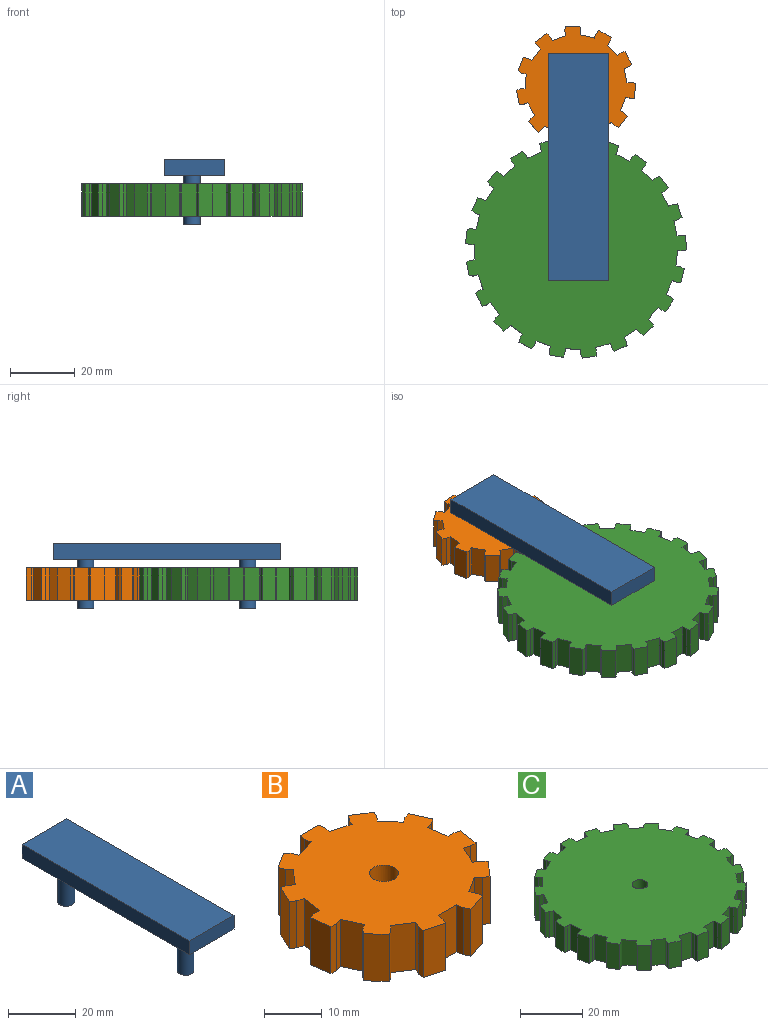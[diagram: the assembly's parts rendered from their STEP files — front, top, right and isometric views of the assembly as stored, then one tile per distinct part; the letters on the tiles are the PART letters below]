
ASSEMBLY  parts=3 mates=2
PART A: 10 faces, bbox 18.7x70.1x20 mm
  f0: plane 18.73x5mm, normal (0,1,0), area 93.7mm2, adj f1,f3,f4,f5
  f1: plane 70.05x5mm, normal (-1,0,0), area 350.3mm2, adj f0,f2,f4,f5
  f2: plane 18.73x5mm, normal (0,-1,0), area 93.7mm2, adj f1,f3,f4,f5
  f3: plane 70.05x5mm, normal (1,0,0), area 350.3mm2, adj f0,f2,f4,f5
  f4: plane 70.05x18.73mm, normal (0,0,1), area 1312.1mm2, adj f0,f1,f2,f3
  f5: plane 70.05x18.73mm, normal (0,0,-1), area 1272.8mm2, adj f0,f1,f2,f3,f6,f8
  f6: cylinder r=2.5mm len=15mm, axis (0,0,1), area 235.6mm2, adj f5,f7
  f7: plane 5x5mm, normal (0,0,-1), area 19.6mm2, adj f6
  f8: cylinder r=2.5mm len=15mm, axis (0,0,1), area 235.6mm2, adj f5,f9
  f9: plane 5x5mm, normal (0,0,-1), area 19.6mm2, adj f8
PART B: 69 faces, bbox 36.9x36.5x10 mm
  f0: plane 10x1.43mm, normal (-0.99,-0.14,0), area 14.5mm2, adj f1,f6,f7,f14
  f1: plane 10x1.18mm, normal (-0.9,-0.43,0), area 13mm2, adj f0,f2,f6,f7
  f2: plane 10x4.31mm, normal (0.28,-0.96,0), area 44.9mm2, adj f1,f3,f6,f7
  f3: plane 10x1.29mm, normal (0.99,0.13,0), area 13mm2, adj f2,f4,f6,f7
  f4: plane 10x1.32mm, normal (0.91,0.42,0), area 14.5mm2, adj f3,f5,f6,f7
  f5: plane 10x3.77mm, normal (0.54,-0.84,0), area 44.8mm2, adj f4,f6,f7,f8
  f6: plane 36.87x36.49mm, normal (0,0,1), area 888.5mm2, adj f0,f1,f2,f3,f4,f5,f8,f9
  f7: plane 36.87x36.49mm, normal (0,0,-1), area 888.5mm2, adj f0,f1,f2,f3,f4,f5,f8,f9
  f8: plane 10x1.09mm, normal (-0.76,-0.65,0), area 14.5mm2, adj f5,f6,f7,f63
  f9: plane 10x1.32mm, normal (-0.91,0.42,0), area 14.5mm2, adj f6,f7,f10,f20
  f10: plane 10x1.29mm, normal (-0.99,0.13,0), area 13mm2, adj f6,f7,f9,f11
  f11: plane 10x4.31mm, normal (-0.28,-0.96,0), area 44.9mm2, adj f6,f7,f10,f12
  f12: plane 10x1.18mm, normal (0.9,-0.43,0), area 13mm2, adj f6,f7,f11,f13
  f13: plane 10x1.43mm, normal (0.99,-0.14,0), area 14.5mm2, adj f6,f7,f12,f14
  f14: plane 10x4.48mm, normal (0,-1,0), area 44.8mm2, adj f0,f6,f7,f13
  f15: plane 10x1.22mm, normal (-0.54,0.84,0), area 14.5mm2, adj f6,f7,f16,f26
  f16: plane 10x0.99mm, normal (-0.76,0.65,0), area 13mm2, adj f6,f7,f15,f17
  f17: plane 10x3.4mm, normal (-0.76,-0.65,0), area 44.9mm2, adj f6,f7,f16,f18
  f18: plane 10x1.1mm, normal (0.53,-0.85,0), area 13mm2, adj f6,f7,f17,f19
  f19: plane 10x1.09mm, normal (0.76,-0.65,0), area 14.5mm2, adj f6,f7,f18,f20
  f20: plane 10x3.77mm, normal (-0.54,-0.84,0), area 44.8mm2, adj f6,f7,f9,f19
  f21: plane 10x1.45mm, normal (0,1,0), area 14.5mm2, adj f6,f7,f22,f32
  f22: plane 10x1.25mm, normal (-0.29,0.96,0), area 13mm2, adj f6,f7,f21,f23
  f23: plane 10x4.45mm, normal (-0.99,-0.14,0), area 44.9mm2, adj f6,f7,f22,f24
  f24: plane 10x1.3mm, normal (-0.01,-1,0), area 13mm2, adj f6,f7,f23,f25
  f25: plane 10x1.39mm, normal (0.28,-0.96,0), area 14.5mm2, adj f6,f7,f24,f26
  f26: plane 10x4.08mm, normal (-0.91,-0.42,0), area 44.8mm2, adj f6,f7,f15,f25
  f27: plane 10x1.22mm, normal (0.54,0.84,0), area 14.5mm2, adj f6,f7,f28,f38
  f28: plane 10x1.25mm, normal (0.27,0.96,0), area 13mm2, adj f6,f7,f27,f29
  f29: plane 10x4.09mm, normal (-0.91,0.42,0), area 44.9mm2, adj f6,f7,f28,f30
  f30: plane 10x1.09mm, normal (-0.55,-0.84,0), area 13mm2, adj f6,f7,f29,f31
  f31: plane 10x1.39mm, normal (-0.28,-0.96,0), area 14.5mm2, adj f6,f7,f30,f32
  f32: plane 10x4.44mm, normal (-0.99,0.14,0), area 44.8mm2, adj f6,f7,f21,f31
  f33: plane 10x1.32mm, normal (0.91,0.42,0), area 14.5mm2, adj f6,f7,f34,f44
  f34: plane 10x0.98mm, normal (0.75,0.66,0), area 13mm2, adj f6,f7,f33,f35
  f35: plane 10x3.78mm, normal (-0.54,0.84,0), area 44.9mm2, adj f6,f7,f34,f36
  f36: plane 10x1.19mm, normal (-0.91,-0.41,0), area 13mm2, adj f6,f7,f35,f37
  f37: plane 10x1.09mm, normal (-0.76,-0.65,0), area 14.5mm2, adj f6,f7,f36,f38
  f38: plane 10x3.39mm, normal (-0.76,0.65,0), area 44.8mm2, adj f6,f7,f27,f37
  f39: plane 10x1.43mm, normal (0.99,-0.14,0), area 14.5mm2, adj f6,f7,f40,f50
  f40: plane 10x1.29mm, normal (0.99,0.15,0), area 13mm2, adj f6,f7,f39,f41
  f41: plane 10x4.49mm, normal (0,1,0), area 44.9mm2, adj f6,f7,f40,f42
  f42: plane 10x1.29mm, normal (-0.99,0.15,0), area 13mm2, adj f6,f7,f41,f43
  f43: plane 10x1.43mm, normal (-0.99,-0.14,0), area 14.5mm2, adj f6,f7,f42,f44
  f44: plane 10x4.3mm, normal (-0.28,0.96,0), area 44.8mm2, adj f6,f7,f33,f43
  f45: plane 10x1.09mm, normal (0.76,-0.65,0), area 14.5mm2, adj f6,f7,f46,f56
  f46: plane 10x1.19mm, normal (0.91,-0.41,0), area 13mm2, adj f6,f7,f45,f47
  f47: plane 10x3.78mm, normal (0.54,0.84,0), area 44.9mm2, adj f6,f7,f46,f48
  f48: plane 10x0.98mm, normal (-0.75,0.66,0), area 13mm2, adj f6,f7,f47,f49
  f49: plane 10x1.32mm, normal (-0.91,0.42,0), area 14.5mm2, adj f6,f7,f48,f50
  f50: plane 10x4.3mm, normal (0.28,0.96,0), area 44.8mm2, adj f6,f7,f39,f49
  f51: plane 10x1.39mm, normal (0.28,-0.96,0), area 14.5mm2, adj f6,f7,f52,f62
  f52: plane 10x1.09mm, normal (0.55,-0.84,0), area 13mm2, adj f6,f7,f51,f53
  f53: plane 10x4.09mm, normal (0.91,0.42,0), area 44.9mm2, adj f6,f7,f52,f54
  f54: plane 10x1.25mm, normal (-0.27,0.96,0), area 13mm2, adj f6,f7,f53,f55
  f55: plane 10x1.22mm, normal (-0.54,0.84,0), area 14.5mm2, adj f6,f7,f54,f56
  f56: plane 10x3.39mm, normal (0.76,0.65,0), area 44.8mm2, adj f6,f7,f45,f55
  f57: plane 10x1.39mm, normal (-0.28,-0.96,0), area 14.5mm2, adj f6,f7,f58,f67
  f58: plane 10x1.3mm, normal (0.01,-1,0), area 13mm2, adj f6,f7,f57,f59
  f59: plane 10x4.45mm, normal (0.99,-0.14,0), area 44.9mm2, adj f6,f7,f58,f60
  f60: plane 10x1.25mm, normal (0.29,0.96,0), area 13mm2, adj f6,f7,f59,f61
  f61: plane 10x1.45mm, normal (0,1,0), area 14.5mm2, adj f6,f7,f60,f62
  f62: plane 10x4.44mm, normal (0.99,0.14,0), area 44.8mm2, adj f6,f7,f51,f61
  f63: plane 10x1.1mm, normal (-0.53,-0.85,0), area 13mm2, adj f6,f7,f8,f64
  f64: plane 10x3.4mm, normal (0.76,-0.65,0), area 44.9mm2, adj f6,f7,f63,f65
  f65: plane 10x0.99mm, normal (0.76,0.65,0), area 13mm2, adj f6,f7,f64,f66
  f66: plane 10x1.22mm, normal (0.54,0.84,0), area 14.5mm2, adj f6,f7,f65,f67
  f67: plane 10x4.08mm, normal (0.91,-0.42,0), area 44.8mm2, adj f6,f7,f57,f66
  f68: cylinder r=2.5mm len=10mm, axis (0,0,-1), area 157.1mm2, adj f6,f7
PART C: 129 faces, bbox 68.1x67.9x10 mm
  f0: plane 10x1.44mm, normal (-1,-0.07,0), area 14.5mm2, adj f1,f5,f6,f7
  f1: plane 10x4.64mm, normal (-0.15,0.99,0), area 46.9mm2, adj f0,f6,f7,f8
  f2: plane 10x1.44mm, normal (1,-0.07,0), area 14.5mm2, adj f3,f6,f7,f10
  f3: plane 10x1.27mm, normal (0.98,0.22,0), area 13mm2, adj f2,f4,f6,f7
  f4: plane 10x4.33mm, normal (0,1,0), area 43.3mm2, adj f3,f5,f6,f7
  f5: plane 10x1.27mm, normal (-0.98,0.22,0), area 13mm2, adj f0,f4,f6,f7
  f6: plane 68.12x67.93mm, normal (0,0,1), area 3328.3mm2, adj f0,f1,f2,f3,f4,f5,f8,f9
  f7: plane 68.12x67.93mm, normal (0,0,-1), area 3328.3mm2, adj f0,f1,f2,f3,f4,f5,f8,f9
  f8: plane 10x1.41mm, normal (0.97,0.22,0), area 14.5mm2, adj f1,f6,f7,f125
  f9: plane 10x1.41mm, normal (-0.97,0.22,0), area 14.5mm2, adj f6,f7,f10,f14
  f10: plane 10x4.64mm, normal (0.15,0.99,0), area 46.9mm2, adj f2,f6,f7,f9
  f11: plane 10x1.35mm, normal (0.93,-0.37,0), area 14.5mm2, adj f6,f7,f12,f16
  f12: plane 10x1.3mm, normal (1,-0.08,0), area 13mm2, adj f6,f7,f11,f13
  f13: plane 10x4.14mm, normal (0.29,0.96,0), area 43.3mm2, adj f6,f7,f12,f14
  f14: plane 10x1.13mm, normal (-0.87,0.5,0), area 13mm2, adj f6,f7,f9,f13
  f15: plane 10x1.25mm, normal (-0.87,0.5,0), area 14.5mm2, adj f6,f7,f16,f20
  f16: plane 10x4.22mm, normal (0.43,0.9,0), area 46.9mm2, adj f6,f7,f11,f15
  f17: plane 10x1.13mm, normal (0.78,-0.62,0), area 14.5mm2, adj f6,f7,f18,f22
  f18: plane 10x1.21mm, normal (0.93,-0.37,0), area 13mm2, adj f6,f7,f17,f19
  f19: plane 10x3.58mm, normal (0.56,0.83,0), area 43.3mm2, adj f6,f7,f18,f20
  f20: plane 10x0.95mm, normal (-0.68,0.73,0), area 13mm2, adj f6,f7,f15,f19
  f21: plane 10x1.06mm, normal (-0.68,0.73,0), area 14.5mm2, adj f6,f7,f22,f26
  f22: plane 10x3.44mm, normal (0.68,0.73,0), area 46.9mm2, adj f6,f7,f17,f21
  f23: plane 10x1.2mm, normal (0.56,-0.83,0), area 14.5mm2, adj f6,f7,f24,f28
  f24: plane 10x1.02mm, normal (0.78,-0.63,0), area 13mm2, adj f6,f7,f23,f25
  f25: plane 10x3.39mm, normal (0.78,0.62,0), area 43.3mm2, adj f6,f7,f24,f26
  f26: plane 10x1.17mm, normal (-0.44,0.9,0), area 13mm2, adj f6,f7,f21,f25
  f27: plane 10x1.3mm, normal (-0.43,0.9,0), area 14.5mm2, adj f6,f7,f28,f32
  f28: plane 10x4.06mm, normal (0.87,0.5,0), area 46.9mm2, adj f6,f7,f23,f27
  f29: plane 10x1.38mm, normal (0.29,-0.96,0), area 14.5mm2, adj f6,f7,f30,f34
  f30: plane 10x1.08mm, normal (0.56,-0.83,0), area 13mm2, adj f6,f7,f29,f31
  f31: plane 10x4.03mm, normal (0.93,0.37,0), area 43.3mm2, adj f6,f7,f30,f32
  f32: plane 10x1.29mm, normal (-0.15,0.99,0), area 13mm2, adj f6,f7,f27,f31
  f33: plane 10x1.43mm, normal (-0.15,0.99,0), area 14.5mm2, adj f6,f7,f34,f38
  f34: plane 10x4.57mm, normal (0.97,0.22,0), area 46.9mm2, adj f6,f7,f29,f33
  f35: plane 10x1.45mm, normal (0,-1,0), area 14.5mm2, adj f6,f7,f36,f40
  f36: plane 10x1.25mm, normal (0.29,-0.96,0), area 13mm2, adj f6,f7,f35,f37
  f37: plane 10x4.32mm, normal (1,0.07,0), area 43.3mm2, adj f6,f7,f36,f38
  f38: plane 10x1.29mm, normal (0.15,0.99,0), area 13mm2, adj f6,f7,f33,f37
  f39: plane 10x1.43mm, normal (0.15,0.99,0), area 14.5mm2, adj f6,f7,f40,f44
  f40: plane 10x4.68mm, normal (1,-0.07,0), area 46.9mm2, adj f6,f7,f35,f39
  f41: plane 10x1.38mm, normal (-0.29,-0.96,0), area 14.5mm2, adj f6,f7,f42,f46
  f42: plane 10x1.31mm, normal (0,-1,0), area 13mm2, adj f6,f7,f41,f43
  f43: plane 10x4.22mm, normal (0.97,-0.22,0), area 43.3mm2, adj f6,f7,f42,f44
  f44: plane 10x1.18mm, normal (0.43,0.9,0), area 13mm2, adj f6,f7,f39,f43
  f45: plane 10x1.3mm, normal (0.43,0.9,0), area 14.5mm2, adj f6,f7,f46,f50
  f46: plane 10x4.36mm, normal (0.93,-0.37,0), area 46.9mm2, adj f6,f7,f41,f45
  f47: plane 10x1.2mm, normal (-0.56,-0.83,0), area 14.5mm2, adj f6,f7,f48,f52
  f48: plane 10x1.25mm, normal (-0.3,-0.95,0), area 13mm2, adj f6,f7,f47,f49
  f49: plane 10x3.75mm, normal (0.87,-0.5,0), area 43.3mm2, adj f6,f7,f48,f50
  f50: plane 10x0.96mm, normal (0.68,0.73,0), area 13mm2, adj f6,f7,f45,f49
  f51: plane 10x1.06mm, normal (0.68,0.73,0), area 14.5mm2, adj f6,f7,f52,f56
  f52: plane 10x3.67mm, normal (0.78,-0.62,0), area 46.9mm2, adj f6,f7,f47,f51
  f53: plane 10x1.13mm, normal (-0.78,-0.62,0), area 14.5mm2, adj f6,f7,f54,f58
  f54: plane 10x1.08mm, normal (-0.57,-0.82,0), area 13mm2, adj f6,f7,f53,f55
  f55: plane 10x3.17mm, normal (0.68,-0.73,0), area 43.3mm2, adj f6,f7,f54,f56
  f56: plane 10x1.13mm, normal (0.86,0.5,0), area 13mm2, adj f6,f7,f51,f55
  f57: plane 10x1.25mm, normal (0.87,0.5,0), area 14.5mm2, adj f6,f7,f58,f62
  f58: plane 10x3.87mm, normal (0.56,-0.83,0), area 46.9mm2, adj f6,f7,f53,f57
  f59: plane 10x1.35mm, normal (-0.93,-0.37,0), area 14.5mm2, adj f6,f7,f60,f64
  f60: plane 10x1.02mm, normal (-0.78,-0.62,0), area 13mm2, adj f6,f7,f59,f61
  f61: plane 10x3.9mm, normal (0.43,-0.9,0), area 43.3mm2, adj f6,f7,f60,f62
  f62: plane 10x1.27mm, normal (0.97,0.22,0), area 13mm2, adj f6,f7,f57,f61
  f63: plane 10x1.41mm, normal (0.97,0.22,0), area 14.5mm2, adj f6,f7,f64,f68
  f64: plane 10x4.48mm, normal (0.29,-0.96,0), area 46.9mm2, adj f6,f7,f59,f63
  f65: plane 10x1.44mm, normal (-1,-0.07,0), area 14.5mm2, adj f6,f7,f66,f70
  f66: plane 10x1.22mm, normal (-0.93,-0.36,0), area 13mm2, adj f6,f7,f65,f67
  f67: plane 10x4.28mm, normal (0.15,-0.99,0), area 43.3mm2, adj f6,f7,f66,f68
  f68: plane 10x1.3mm, normal (1,-0.07,0), area 13mm2, adj f6,f7,f63,f67
  f69: plane 10x1.44mm, normal (1,-0.07,0), area 14.5mm2, adj f6,f7,f70,f74
  f70: plane 10x4.69mm, normal (0,-1,0), area 46.9mm2, adj f6,f7,f65,f69
  f71: plane 10x1.41mm, normal (-0.97,0.22,0), area 14.5mm2, adj f6,f7,f72,f76
  f72: plane 10x1.3mm, normal (-1,-0.07,0), area 13mm2, adj f6,f7,f71,f73
  f73: plane 10x4.28mm, normal (-0.15,-0.99,0), area 43.3mm2, adj f6,f7,f72,f74
  f74: plane 10x1.22mm, normal (0.93,-0.36,0), area 13mm2, adj f6,f7,f69,f73
  f75: plane 10x1.35mm, normal (0.93,-0.37,0), area 14.5mm2, adj f6,f7,f76,f80
  f76: plane 10x4.48mm, normal (-0.29,-0.96,0), area 46.9mm2, adj f6,f7,f71,f75
  f77: plane 10x1.25mm, normal (-0.87,0.5,0), area 14.5mm2, adj f6,f7,f78,f82
  f78: plane 10x1.27mm, normal (-0.97,0.22,0), area 13mm2, adj f6,f7,f77,f79
  f79: plane 10x3.9mm, normal (-0.43,-0.9,0), area 43.3mm2, adj f6,f7,f78,f80
  f80: plane 10x1.02mm, normal (0.78,-0.62,0), area 13mm2, adj f6,f7,f75,f79
  f81: plane 10x1.13mm, normal (0.78,-0.62,0), area 14.5mm2, adj f6,f7,f82,f86
  f82: plane 10x3.87mm, normal (-0.56,-0.83,0), area 46.9mm2, adj f6,f7,f77,f81
  f83: plane 10x1.06mm, normal (-0.68,0.73,0), area 14.5mm2, adj f6,f7,f84,f88
  f84: plane 10x1.13mm, normal (-0.86,0.5,0), area 13mm2, adj f6,f7,f83,f85
  f85: plane 10x3.17mm, normal (-0.68,-0.73,0), area 43.3mm2, adj f6,f7,f84,f86
  f86: plane 10x1.08mm, normal (0.57,-0.82,0), area 13mm2, adj f6,f7,f81,f85
  f87: plane 10x1.2mm, normal (0.56,-0.83,0), area 14.5mm2, adj f6,f7,f88,f92
  f88: plane 10x3.67mm, normal (-0.78,-0.62,0), area 46.9mm2, adj f6,f7,f83,f87
  f89: plane 10x1.3mm, normal (-0.43,0.9,0), area 14.5mm2, adj f6,f7,f90,f94
  f90: plane 10x0.96mm, normal (-0.68,0.73,0), area 13mm2, adj f6,f7,f89,f91
  f91: plane 10x3.75mm, normal (-0.87,-0.5,0), area 43.3mm2, adj f6,f7,f90,f92
  f92: plane 10x1.25mm, normal (0.3,-0.95,0), area 13mm2, adj f6,f7,f87,f91
  f93: plane 10x1.38mm, normal (0.29,-0.96,0), area 14.5mm2, adj f6,f7,f94,f98
  f94: plane 10x4.36mm, normal (-0.93,-0.37,0), area 46.9mm2, adj f6,f7,f89,f93
  f95: plane 10x1.43mm, normal (-0.15,0.99,0), area 14.5mm2, adj f6,f7,f96,f100
  f96: plane 10x1.18mm, normal (-0.43,0.9,0), area 13mm2, adj f6,f7,f95,f97
  f97: plane 10x4.22mm, normal (-0.97,-0.22,0), area 43.3mm2, adj f6,f7,f96,f98
  f98: plane 10x1.31mm, normal (0,-1,0), area 13mm2, adj f6,f7,f93,f97
  f99: plane 10x1.45mm, normal (0,-1,0), area 14.5mm2, adj f6,f7,f100,f104
  f100: plane 10x4.68mm, normal (-1,-0.07,0), area 46.9mm2, adj f6,f7,f95,f99
  f101: plane 10x1.43mm, normal (0.15,0.99,0), area 14.5mm2, adj f6,f7,f102,f106
  f102: plane 10x1.29mm, normal (-0.15,0.99,0), area 13mm2, adj f6,f7,f101,f103
  f103: plane 10x4.32mm, normal (-1,0.07,0), area 43.3mm2, adj f6,f7,f102,f104
  f104: plane 10x1.25mm, normal (-0.29,-0.96,0), area 13mm2, adj f6,f7,f99,f103
  f105: plane 10x1.38mm, normal (-0.29,-0.96,0), area 14.5mm2, adj f6,f7,f106,f110
  f106: plane 10x4.57mm, normal (-0.97,0.22,0), area 46.9mm2, adj f6,f7,f101,f105
  f107: plane 10x1.3mm, normal (0.43,0.9,0), area 14.5mm2, adj f6,f7,f108,f112
  f108: plane 10x1.29mm, normal (0.15,0.99,0), area 13mm2, adj f6,f7,f107,f109
  f109: plane 10x4.03mm, normal (-0.93,0.37,0), area 43.3mm2, adj f6,f7,f108,f110
  f110: plane 10x1.08mm, normal (-0.56,-0.83,0), area 13mm2, adj f6,f7,f105,f109
  f111: plane 10x1.2mm, normal (-0.56,-0.83,0), area 14.5mm2, adj f6,f7,f112,f116
  f112: plane 10x4.06mm, normal (-0.87,0.5,0), area 46.9mm2, adj f6,f7,f107,f111
  f113: plane 10x1.06mm, normal (0.68,0.73,0), area 14.5mm2, adj f6,f7,f114,f118
  f114: plane 10x1.17mm, normal (0.44,0.9,0), area 13mm2, adj f6,f7,f113,f115
  f115: plane 10x3.39mm, normal (-0.78,0.62,0), area 43.3mm2, adj f6,f7,f114,f116
  f116: plane 10x1.02mm, normal (-0.78,-0.63,0), area 13mm2, adj f6,f7,f111,f115
  f117: plane 10x1.13mm, normal (-0.78,-0.62,0), area 14.5mm2, adj f6,f7,f118,f122
  f118: plane 10x3.44mm, normal (-0.68,0.73,0), area 46.9mm2, adj f6,f7,f113,f117
  f119: plane 10x1.25mm, normal (0.87,0.5,0), area 14.5mm2, adj f6,f7,f120,f124
  f120: plane 10x0.95mm, normal (0.68,0.73,0), area 13mm2, adj f6,f7,f119,f121
  f121: plane 10x3.58mm, normal (-0.56,0.83,0), area 43.3mm2, adj f6,f7,f120,f122
  f122: plane 10x1.21mm, normal (-0.93,-0.37,0), area 13mm2, adj f6,f7,f117,f121
  f123: plane 10x1.35mm, normal (-0.93,-0.37,0), area 14.5mm2, adj f6,f7,f124,f127
  f124: plane 10x4.22mm, normal (-0.43,0.9,0), area 46.9mm2, adj f6,f7,f119,f123
  f125: plane 10x1.13mm, normal (0.87,0.5,0), area 13mm2, adj f6,f7,f8,f126
  f126: plane 10x4.14mm, normal (-0.29,0.96,0), area 43.3mm2, adj f6,f7,f125,f127
  f127: plane 10x1.3mm, normal (-1,-0.08,0), area 13mm2, adj f6,f7,f123,f126
  f128: cylinder r=2.5mm len=10mm, axis (0,0,-1), area 157.1mm2, adj f6,f7
PLACE A t=(-14.72,-19.57,10.32)mm fixed
PLACE B rot(axis=(0,0,-1),29.4deg) t=(-39.29,-13.12,-2.18)mm
PLACE C rot(axis=(0,0,1),118.3deg) t=(-14.72,-19.57,-2.18)mm
MATE revolute B.f68 <-> A.f6  axis (0,0,-1) through (-14.72,30.43,2.82)mm
MATE revolute C.f128 <-> A.f8  axis (0,0,-1) through (-14.72,-19.57,2.82)mm
